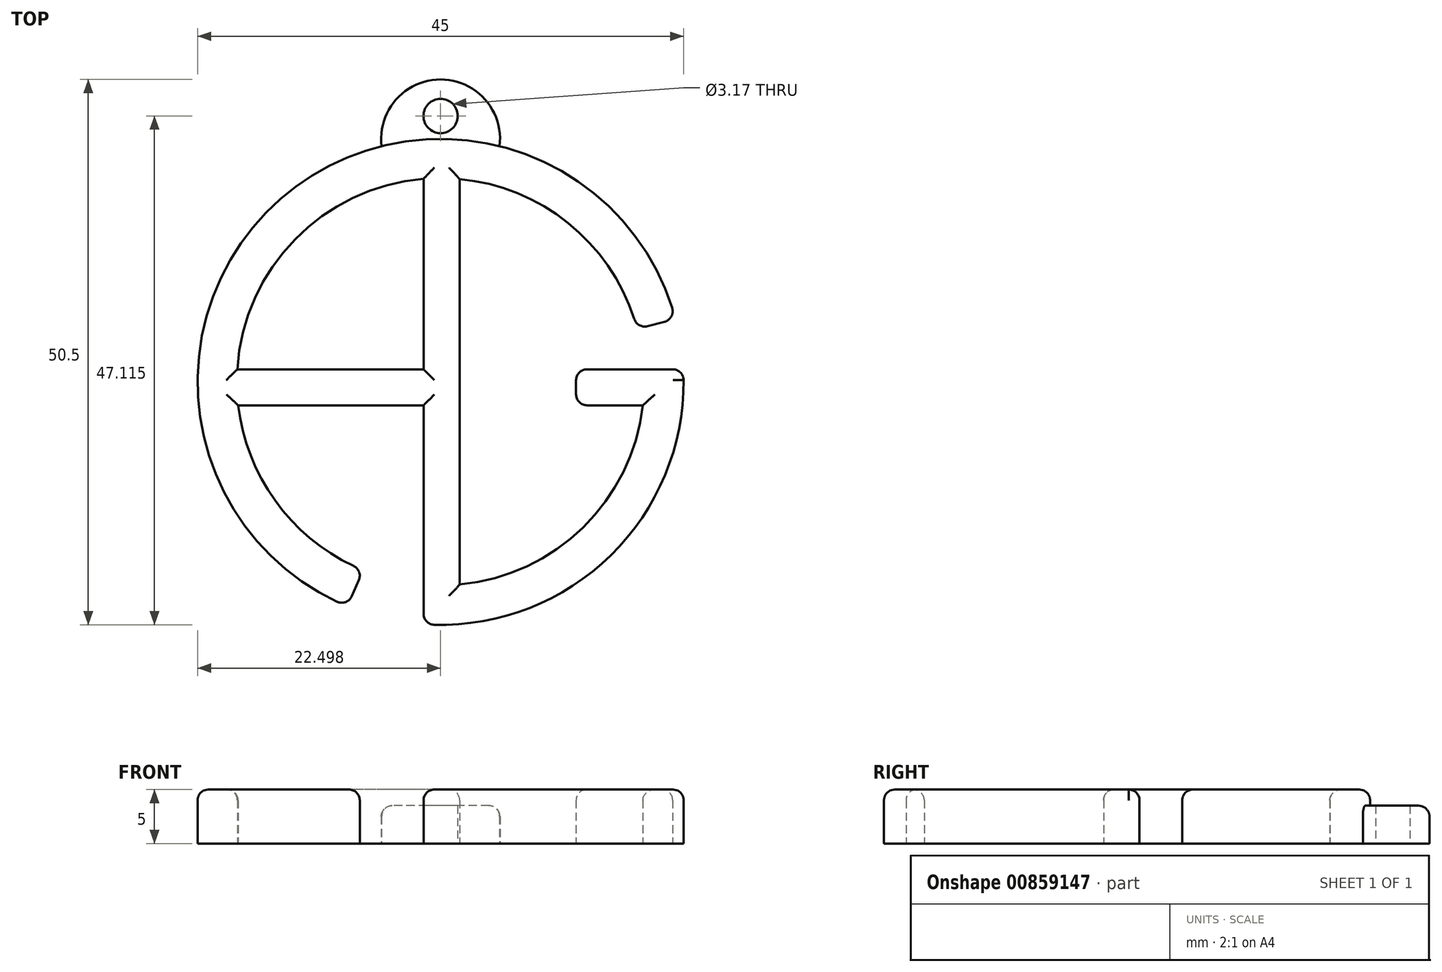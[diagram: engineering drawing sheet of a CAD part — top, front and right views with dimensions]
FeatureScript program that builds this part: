
annotation { "Feature Type Name" : "Feature", "Feature Type Description" : "" }
export const myFeature = defineFeature(function(context is Context, id is Id, definition is map)
    precondition{}
    {
        {
            var Q0;
            Q0=qCreatedBy(makeId("Top.planeOp"),FACE);
            var sketch = newSketch(context, id + "F0", { "sketchPlane" : qUnion([Q0])});
            skArc(sketch, "E0", {"start": v(14.96, 4.5) * mm, "mid": v(-21.6, 15.6) * mm, "end": v(-15.4, -22.1) * mm});
            skArc(sketch, "E1", {"start": v(11.44, 3.57) * mm, "mid": v(5.39, 13.08) * mm, "end": v(-5, 17.44) * mm});
            skLineSegment(sketch, "E2", {"start": v(-8.35, 17.46) * mm, "end": v(-8.35, -0.18) * mm});
            skLineSegment(sketch, "E3", {"start": v(-5, 17.44) * mm, "end": v(-5, -20.1) * mm});
            skLineSegment(sketch, "E4", {"start": v(12.05, -0.18) * mm, "end": v(5.77, -0.18) * mm});
            skLineSegment(sketch, "E5", {"start": v(-25.5, -3.5) * mm, "end": v(-8.35, -3.5) * mm});
            skLineSegment(sketch, "E6.trimOffspring", {"start": v(-8.35, -0.18) * mm, "end": v(-25.6, -0.18) * mm});
            skLineSegment(sketch, "E7.trimOffspring", {"start": v(-8.35, -3.5) * mm, "end": v(-8.35, -20.12) * mm});
            skLineSegment(sketch, "E8", {"start": v(5.77, -0.18) * mm, "end": v(5.77, -3.5) * mm});
            skLineSegment(sketch, "E9.trimOffspring", {"start": v(5.77, -3.5) * mm, "end": v(11.96, -3.5) * mm});
            skLineSegment(sketch, "E10", {"start": v(-13.94, -18.77) * mm, "end": v(-15.4, -22.1) * mm});
            skLineSegment(sketch, "E11", {"start": v(-8.35, -20.12) * mm, "end": v(-8.35, -23.77) * mm});
            skLineSegment(sketch, "E12", {"start": v(11.44, 3.57) * mm, "end": v(14.96, 4.5) * mm});
            skLineSegment(sketch, "E13", {"start": v(12.05, -0.18) * mm, "end": v(15.7, -0.18) * mm});
            skArc(sketch, "E14.trimOffspring", {"start": v(-5, -20.1) * mm, "mid": v(6.42, -14.8) * mm, "end": v(11.96, -3.5) * mm});
            skArc(sketch, "E15.trimOffspring", {"start": v(-8.35, -23.77) * mm, "mid": v(8.99, -17.39) * mm, "end": v(15.7, -0.18) * mm});
            skArc(sketch, "E16", {"start": v(-1.31, 20.5) * mm, "mid": v(-6.77, 26.67) * mm, "end": v(-12.23, 20.5) * mm});
            skCircle(sketch, "E17", {"center": v(-6.77, 23.29) * mm, "radius": 1.59 * mm});
            skArc(sketch, "E18.trimOffspring", {"start": v(-8.35, 17.46) * mm, "mid": v(-20.26, 11.85) * mm, "end": v(-25.6, -0.18) * mm});
            skArc(sketch, "E19.trimOffspring", {"start": v(-25.5, -3.5) * mm, "mid": v(-21.8, -12.71) * mm, "end": v(-13.94, -18.77) * mm});
            skSolve(sketch);
        }
        {
            var Q0;
            Q0=makeQuery(id+"F0.imprint","IMPRINT",FACE,{"disambiguationData":[TD([[makeQuery(id+"F0.imprint","IMPRINT",EDGE,{"derivedFrom":sQuery(id+"F0.wireOp",EDGE,"E1")}),-1.0]])]});
            extrude(context, id + "F1", {"entities" : qUnion([Q0]), "depth" : 5 * mm, "offsetDistance" : 25 * mm});
        }
        {
            var Q0;
            {var subQ0=sQuery(id+"F0.wireOp",EDGE,"E16");Q0=makeQuery(id+"F0.imprint","IMPRINT",FACE,{"disambiguationData":[TD([[makeQuery(id+"F0.imprint","IMPRINT",EDGE,{"derivedFrom":subQ0}),1.0]])]});}
            extrude(context, id + "F2", {"entities" : qUnion([Q0]), "operationType" : NewBodyOperationType.ADD, "depth" : 3.5 * mm, "offsetDistance" : 25 * mm});
        }
        {
            var Q0;
            Q0=makeQuery(id+"F1.opExtrude","CAP_EDGE",EDGE,{"disambiguationData":[OSD([sQuery(id+"F0.wireOp",EDGE,"E0")])],"isStart":false});
            var Q1;
            Q1=makeQuery(id+"F1.opExtrude","CAP_EDGE",EDGE,{"disambiguationData":[OSD([sQuery(id+"F0.wireOp",EDGE,"E1")])],"isStart":false});
            var Q2;
            Q2=makeQuery(id+"F1.opExtrude","CAP_EDGE",EDGE,{"disambiguationData":[OSD([sQuery(id+"F0.wireOp",EDGE,"E12")])],"isStart":false});
            var Q3;
            Q3=makeQuery(id+"F1.opExtrude","CAP_EDGE",EDGE,{"disambiguationData":[OSD([sQuery(id+"F0.wireOp",EDGE,"E4"),sQuery(id+"F0.wireOp",EDGE,"E13")])],"isStart":false});
            var Q4;
            Q4=makeQuery(id+"F1.opExtrude","CAP_EDGE",EDGE,{"disambiguationData":[OSD([sQuery(id+"F0.wireOp",EDGE,"E15.trimOffspring")])],"isStart":false});
            var Q5;
            Q5=makeQuery(id+"F1.opExtrude","CAP_EDGE",EDGE,{"disambiguationData":[OSD([sQuery(id+"F0.wireOp",EDGE,"E9.trimOffspring")])],"isStart":false});
            var Q6;
            Q6=makeQuery(id+"F1.opExtrude","CAP_EDGE",EDGE,{"disambiguationData":[OSD([sQuery(id+"F0.wireOp",EDGE,"E14.trimOffspring")])],"isStart":false});
            var Q7;
            Q7=makeQuery(id+"F1.opExtrude","CAP_EDGE",EDGE,{"disambiguationData":[OSD([sQuery(id+"F0.wireOp",EDGE,"E8")])],"isStart":false});
            var Q8;
            Q8=makeQuery(id+"F1.opExtrude","CAP_EDGE",EDGE,{"disambiguationData":[OSD([sQuery(id+"F0.wireOp",EDGE,"E3")])],"isStart":false});
            var Q9;
            Q9=makeQuery(id+"F1.opExtrude","CAP_EDGE",EDGE,{"disambiguationData":[OSD([sQuery(id+"F0.wireOp",EDGE,"E7.trimOffspring"),sQuery(id+"F0.wireOp",EDGE,"E11")])],"isStart":false});
            var Q10;
            Q10=makeQuery(id+"F1.opExtrude","CAP_EDGE",EDGE,{"disambiguationData":[OSD([sQuery(id+"F0.wireOp",EDGE,"E5")])],"isStart":false});
            var Q11;
            Q11=makeQuery(id+"F1.opExtrude","CAP_EDGE",EDGE,{"disambiguationData":[OSD([sQuery(id+"F0.wireOp",EDGE,"E6.trimOffspring")])],"isStart":false});
            var Q12;
            Q12=makeQuery(id+"F1.opExtrude","CAP_EDGE",EDGE,{"disambiguationData":[OSD([sQuery(id+"F0.wireOp",EDGE,"E2")])],"isStart":false});
            var Q13;
            Q13=makeQuery(id+"F1.opExtrude","CAP_EDGE",EDGE,{"disambiguationData":[OSD([sQuery(id+"F0.wireOp",EDGE,"E18.trimOffspring")])],"isStart":false});
            var Q14;
            Q14=makeQuery(id+"F1.opExtrude","CAP_EDGE",EDGE,{"disambiguationData":[OSD([sQuery(id+"F0.wireOp",EDGE,"E19.trimOffspring")])],"isStart":false});
            var Q15;
            Q15=makeQuery(id+"F1.opExtrude","CAP_EDGE",EDGE,{"disambiguationData":[OSD([sQuery(id+"F0.wireOp",EDGE,"E10")])],"isStart":false});
            fillet(context, id + "F3", {"entities" : qUnion([Q0, Q1, Q2, Q3, Q4, Q5, Q6, Q7, Q8, Q9, Q10, Q11, Q12, Q13, Q14, Q15]), "radius" : 1 * mm, "tangentPropagation" : true, "allowEdgeOverflow" : false});
        }
        {
            var Q0;
            Q0=makeQuery(id+"F1.opExtrude","SWEPT_EDGE",EDGE,{"disambiguationData":[OSD([sQuery(id+"F0.wireOp",EDGE,"E0"),sQuery(id+"F0.wireOp",EDGE,"E10")])]});
            var Q1;
            Q1=makeQuery(id+"F1.opExtrude","SWEPT_EDGE",EDGE,{"disambiguationData":[OSD([sQuery(id+"F0.wireOp",EDGE,"E10"),sQuery(id+"F0.wireOp",EDGE,"E19.trimOffspring")])]});
            var Q2;
            Q2=makeQuery(id+"F1.opExtrude","SWEPT_EDGE",EDGE,{"disambiguationData":[OSD([sQuery(id+"F0.wireOp",EDGE,"E11"),sQuery(id+"F0.wireOp",EDGE,"E15.trimOffspring")])]});
            var Q3;
            Q3=makeQuery(id+"F1.opExtrude","SWEPT_EDGE",EDGE,{"disambiguationData":[OSD([sQuery(id+"F0.wireOp",EDGE,"E8"),sQuery(id+"F0.wireOp",EDGE,"E9.trimOffspring")])]});
            var Q4;
            Q4=makeQuery(id+"F1.opExtrude","SWEPT_EDGE",EDGE,{"disambiguationData":[OSD([sQuery(id+"F0.wireOp",EDGE,"E4"),sQuery(id+"F0.wireOp",EDGE,"E8")])]});
            var Q5;
            Q5=makeQuery(id+"F1.opExtrude","SWEPT_EDGE",EDGE,{"disambiguationData":[OSD([sQuery(id+"F0.wireOp",EDGE,"E13"),sQuery(id+"F0.wireOp",EDGE,"E15.trimOffspring")])]});
            var Q6;
            Q6=makeQuery(id+"F1.opExtrude","SWEPT_EDGE",EDGE,{"disambiguationData":[OSD([sQuery(id+"F0.wireOp",EDGE,"E0"),sQuery(id+"F0.wireOp",EDGE,"E12")])]});
            var Q7;
            Q7=makeQuery(id+"F1.opExtrude","SWEPT_EDGE",EDGE,{"disambiguationData":[OSD([sQuery(id+"F0.wireOp",EDGE,"E1"),sQuery(id+"F0.wireOp",EDGE,"E12")])]});
            fillet(context, id + "F4", {"entities" : qUnion([Q0, Q1, Q2, Q3, Q4, Q5, Q6, Q7]), "radius" : 1 * mm, "tangentPropagation" : true, "allowEdgeOverflow" : false});
        }
        {
            var Q0;
            Q0=makeQuery(id+"F2.opExtrude","CAP_EDGE",EDGE,{"disambiguationData":[OSD([sQuery(id+"F0.wireOp",EDGE,"E16")])],"isStart":false});
            fillet(context, id + "F5", {"entities" : qUnion([Q0]), "radius" : 1 * mm, "tangentPropagation" : true, "allowEdgeOverflow" : false});
        }
    });
